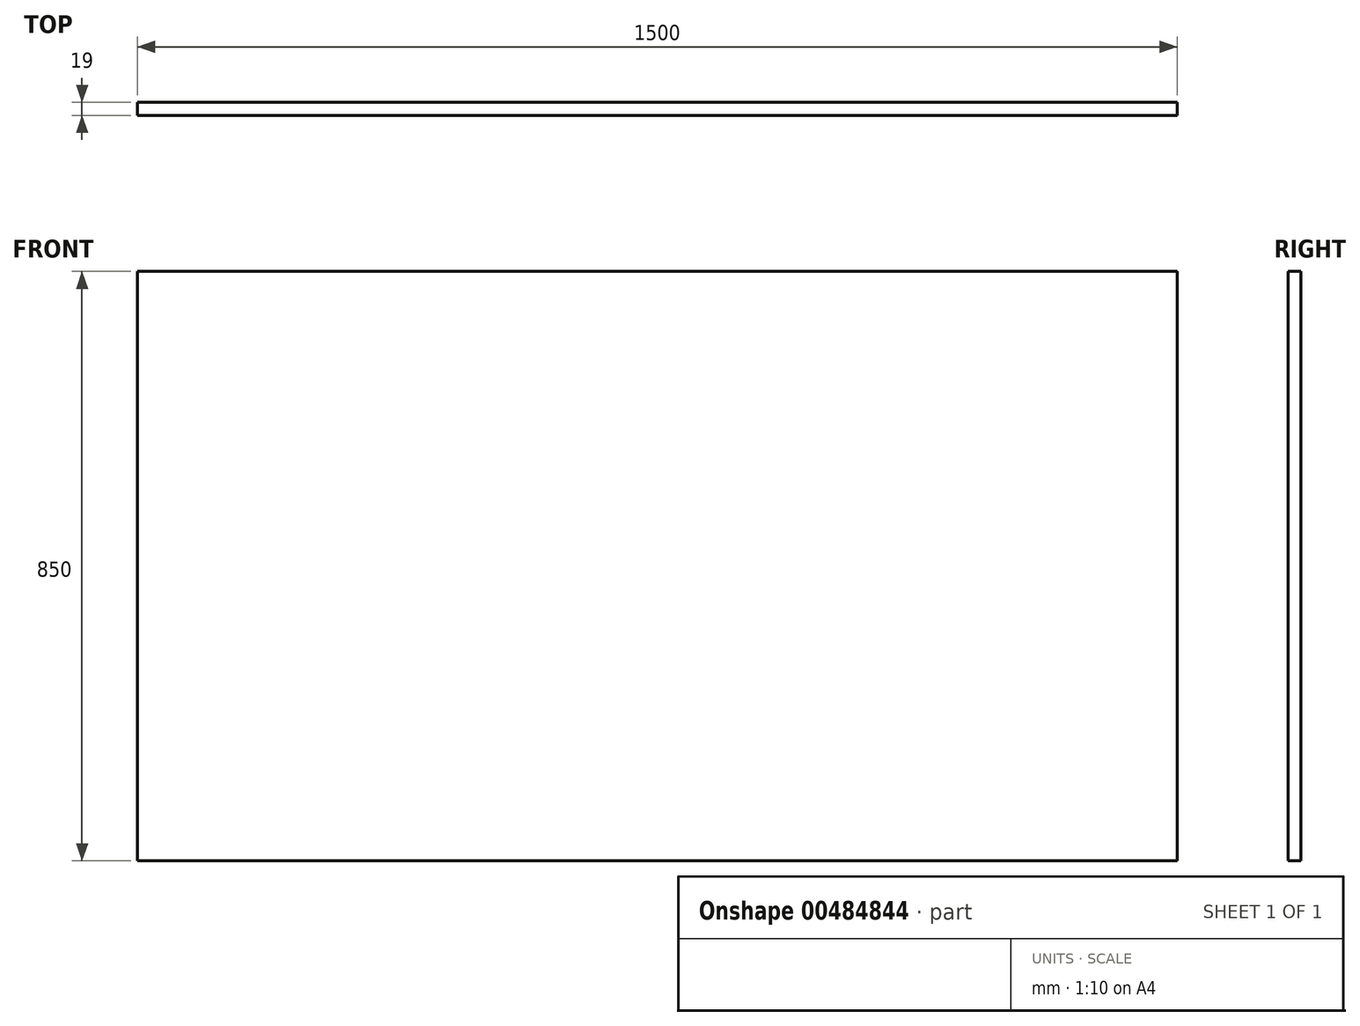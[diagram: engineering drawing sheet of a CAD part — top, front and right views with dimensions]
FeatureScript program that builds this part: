
annotation { "Feature Type Name" : "Feature", "Feature Type Description" : "" }
export const myFeature = defineFeature(function(context is Context, id is Id, definition is map)
    precondition{}
    {
        {
            var Q0;
            Q0=qCreatedBy(makeId("Front.planeOp"),FACE);
            var sketch = newSketch(context, id + "F0", { "sketchPlane" : qUnion([Q0])});
            skLineSegment(sketch, "E0.bottom", {"start": v(-686.98, 612.22) * mm, "end": v(813.02, 612.22) * mm});
            skLineSegment(sketch, "E0.top", {"start": v(-686.98, -237.78) * mm, "end": v(813.02, -237.78) * mm});
            skLineSegment(sketch, "E0.left", {"start": v(-686.98, 612.22) * mm, "end": v(-686.98, -237.78) * mm});
            skLineSegment(sketch, "E0.right", {"start": v(813.02, 612.22) * mm, "end": v(813.02, -237.78) * mm});
            skSolve(sketch);
        }
        {
            var Q0;
            Q0 = qSketchRegion(id + "F0", true);
            extrude(context, id + "F1", {"entities" : qUnion([Q0]), "depth" : 19 * mm});
        }
    });
